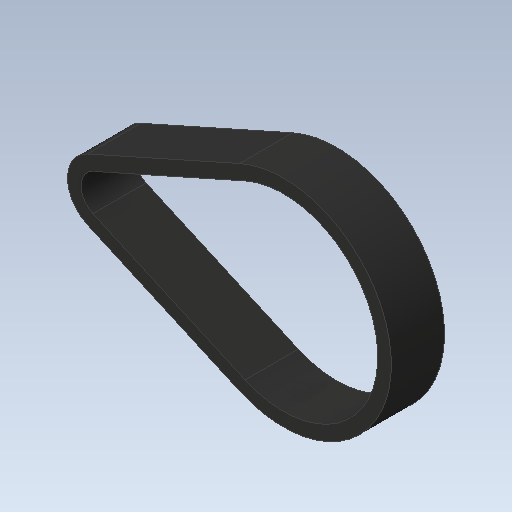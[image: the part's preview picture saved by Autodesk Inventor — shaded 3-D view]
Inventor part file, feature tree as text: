
AUTODESK INVENTOR PART (.ipt)
format: ipt  version: 2020.1 (Build 241239000, 239)  size: 123,392 bytes
history: native  units: mm
features: extrude x1, sketch x1
ambient origin geometry x8: Origin, YZ Plane, XZ Plane, XY Plane, X Axis, Y Axis, Z Axis, Center Point
bodies: Solid1 (feature_tree)
feature tree (2):
  extrude  "Extrusion1"  Depth=51.5mm
  sketch  "Sketch1"  dims[d0=14.52mm d1=51.5mm d4=56.53mm d8=15.0mm d9=0.0mm d10=3.81mm d12=3.81mm d13=1.601mm d14=1.631mm]
